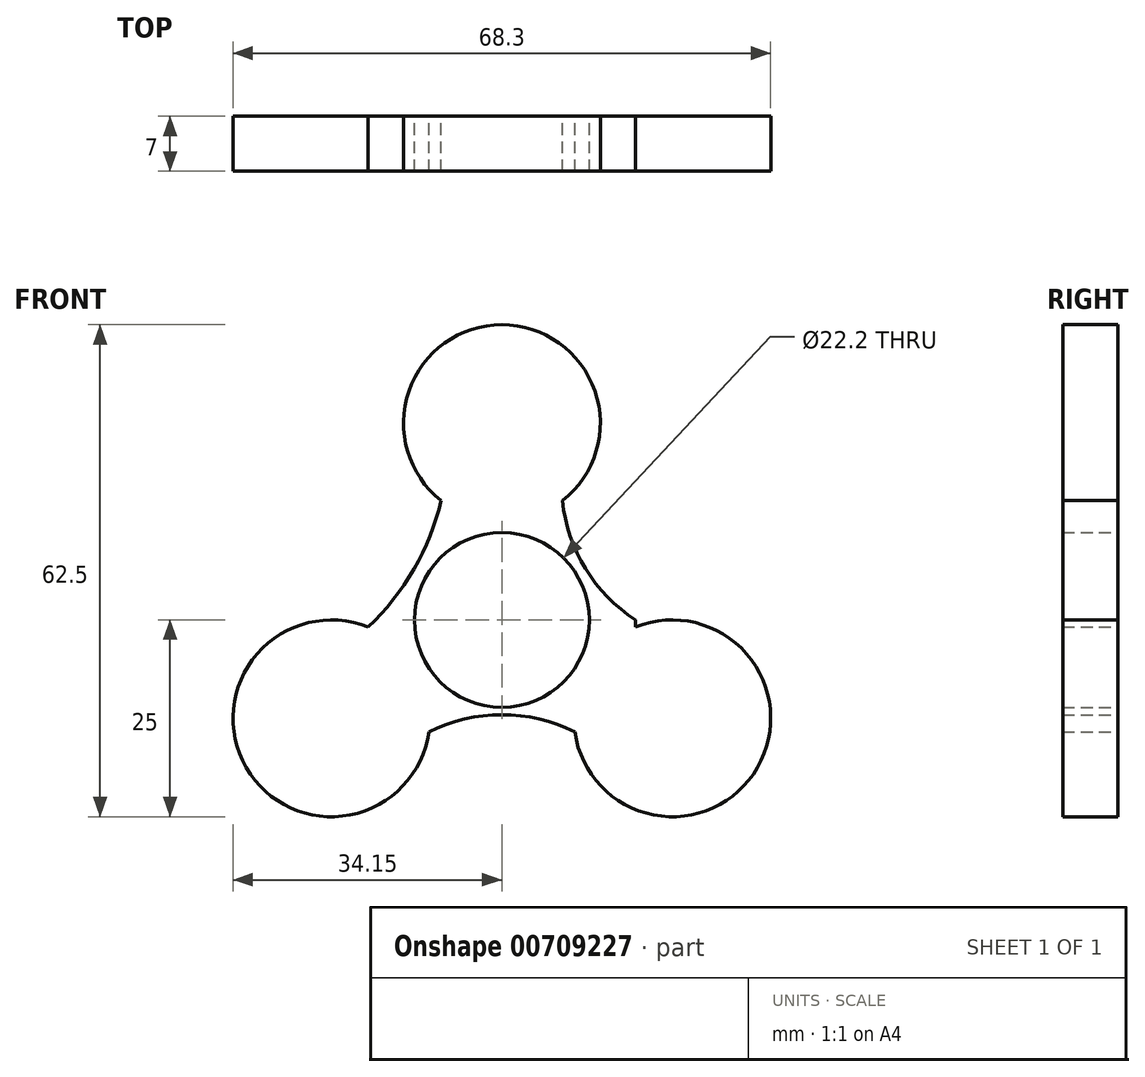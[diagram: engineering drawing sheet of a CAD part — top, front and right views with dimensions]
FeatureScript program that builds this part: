
annotation { "Feature Type Name" : "Feature", "Feature Type Description" : "" }
export const myFeature = defineFeature(function(context is Context, id is Id, definition is map)
    precondition{}
    {
        {
            var Q0;
            Q0=qCreatedBy(makeId("Front.planeOp"),FACE);
            var sketch = newSketch(context, id + "F0", { "sketchPlane" : qUnion([Q0])});
            skCircle(sketch, "E0", {"center": v(0, 0) * mm, "radius": 11.1 * mm});
            skCircle(sketch, "E1", {"center": v(0, 25) * mm, "radius": 11.1 * mm});
            skCircle(sketch, "E2.1.0", {"center": v(-21.65, -12.5) * mm, "radius": 11.1 * mm});
            skCircle(sketch, "E2.2.0", {"center": v(21.65, -12.5) * mm, "radius": 11.1 * mm});
            skArc(sketch, "E3", {"start": v(7.7, 15.15) * mm, "mid": v(0, 37.5) * mm, "end": v(-7.7, 15.16) * mm});
            skArc(sketch, "E4.1.0", {"start": v(-16.98, -0.9) * mm, "mid": v(-32.48, -18.75) * mm, "end": v(-9.27, -14.25) * mm});
            skArc(sketch, "E4.2.0", {"start": v(9.27, -14.25) * mm, "mid": v(32.48, -18.75) * mm, "end": v(16.98, -0.9) * mm});
            skArc(sketch, "E5", {"start": v(-6.23, 15.82) * mm, "mid": v(-6.98, 15.5) * mm, "end": v(-7.7, 15.15) * mm});
            skArc(sketch, "E6.trimOffspring", {"start": v(-10.58, -13.3) * mm, "mid": v(-9.94, -13.8) * mm, "end": v(-9.27, -14.25) * mm});
            skArc(sketch, "E7.trimOffspring", {"start": v(-16.98, -0.9) * mm, "mid": v(-16.91, -1.71) * mm, "end": v(-16.81, -2.5) * mm});
            skArc(sketch, "E8.trimOffspring", {"start": v(7.7, 15.16) * mm, "mid": v(6.98, 15.5) * mm, "end": v(6.23, 15.82) * mm});
            skArc(sketch, "E9.trimOffspring", {"start": v(9.27, -14.25) * mm, "mid": v(9.94, -13.8) * mm, "end": v(10.58, -13.3) * mm});
            skArc(sketch, "E10.trimOffspring", {"start": v(16.81, -2.5) * mm, "mid": v(16.95, -1.26) * mm, "end": v(17, 0) * mm});
            skArc(sketch, "E11", {"start": v(7.7, 15.15) * mm, "mid": v(10.63, 6.52) * mm, "end": v(17, 0) * mm});
            skArc(sketch, "E12", {"start": v(9.27, -14.25) * mm, "mid": v(0, -12.04) * mm, "end": v(-9.27, -14.25) * mm});
            skArc(sketch, "E13", {"start": v(-16.98, -0.9) * mm, "mid": v(-11.18, 6.46) * mm, "end": v(-7.7, 15.16) * mm});
            skSolve(sketch);
        }
        {
            var Q0;
            Q0=makeQuery(id+"F0.imprint","IMPRINT",FACE,{"disambiguationData":[TD([[makeQuery(id+"F0.imprint","IMPRINT",EDGE,{"derivedFrom":sQuery(id+"F0.wireOp",EDGE,"E0")}),-1.0]])]});
            var Q1;
            {var subQ0=sQuery(id+"F0.wireOp",EDGE,"E1");var subQ1=makeQuery(id+"F0.imprint","INTERSECT",VERTEX,{"derivedFrom":[subQ0,sQuery(id+"F0.wireOp",EDGE,"E5")]});Q1=makeQuery(id+"F0.imprint","IMPRINT",FACE,{"disambiguationData":[TD([[makeQuery(id+"F0.imprint","IMPRINT",EDGE,{"disambiguationData":[TD([[subQ1,-1.0]])],"derivedFrom":subQ0}),1.0]])]});}
            var Q2;
            Q2=makeQuery(id+"F0.imprint","IMPRINT",FACE,{"disambiguationData":[TD([[makeQuery(id+"F0.imprint","IMPRINT",EDGE,{"derivedFrom":sQuery(id+"F0.wireOp",EDGE,"E3")}),1.0]])]});
            var Q3;
            Q3=makeQuery(id+"F0.imprint","IMPRINT",FACE,{"disambiguationData":[TD([[makeQuery(id+"F0.imprint","IMPRINT",EDGE,{"derivedFrom":sQuery(id+"F0.wireOp",EDGE,"E4.1.0")}),1.0]])]});
            var Q4;
            {var subQ4=sQuery(id+"F0.wireOp",EDGE,"E4.2.0");Q4=makeQuery(id+"F0.imprint","IMPRINT",FACE,{"disambiguationData":[TD([[makeQuery(id+"F0.imprint","IMPRINT",EDGE,{"derivedFrom":subQ4}),1.0]])]});}
            var Q5;
            {var subQ0=sQuery(id+"F0.wireOp",EDGE,"E2.1.0");var subQ1=makeQuery(id+"F0.imprint","INTERSECT",VERTEX,{"derivedFrom":[subQ0,sQuery(id+"F0.wireOp",EDGE,"E6.trimOffspring")]});Q5=makeQuery(id+"F0.imprint","IMPRINT",FACE,{"disambiguationData":[TD([[makeQuery(id+"F0.imprint","IMPRINT",EDGE,{"disambiguationData":[TD([[subQ1,-1.0]])],"derivedFrom":subQ0}),1.0]])]});}
            var Q6;
            {var subQ0=sQuery(id+"F0.wireOp",EDGE,"E2.2.0");var subQ1=makeQuery(id+"F0.imprint","INTERSECT",VERTEX,{"derivedFrom":[subQ0,sQuery(id+"F0.wireOp",EDGE,"E9.trimOffspring")]});Q6=makeQuery(id+"F0.imprint","IMPRINT",FACE,{"disambiguationData":[TD([[makeQuery(id+"F0.imprint","IMPRINT",EDGE,{"disambiguationData":[TD([[subQ1,1.0]])],"derivedFrom":subQ0}),1.0]])]});}
            extrude(context, id + "F1", {"entities" : qUnion([Q0, Q1, Q2, Q3, Q4, Q5, Q6]), "depth" : 7 * mm, "offsetDistance" : 25 * mm});
        }
    });
